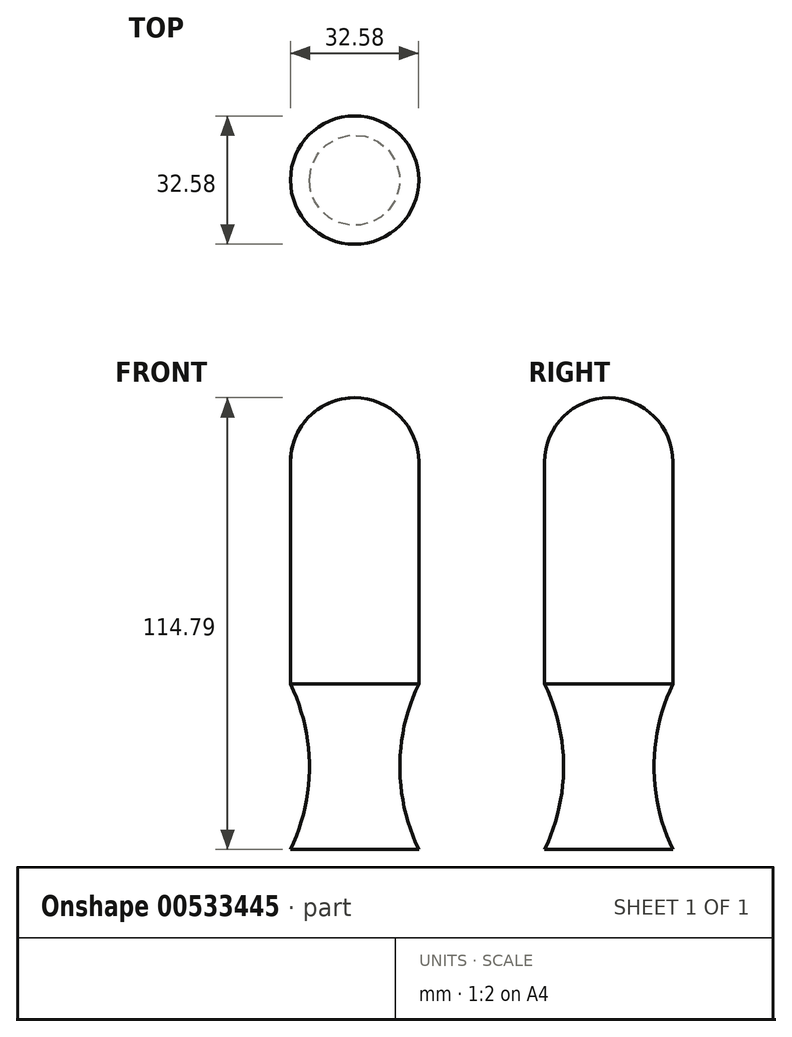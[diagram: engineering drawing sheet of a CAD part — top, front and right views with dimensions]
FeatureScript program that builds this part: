
annotation { "Feature Type Name" : "Feature", "Feature Type Description" : "" }
export const myFeature = defineFeature(function(context is Context, id is Id, definition is map)
    precondition{}
    {
        {
            var Q0;
            Q0=qCreatedBy(makeId("Front.planeOp"),FACE);
            var sketch = newSketch(context, id + "F0", { "sketchPlane" : qUnion([Q0])});
            skLineSegment(sketch, "E0", {"start": v(-16.3, 42.8) * mm, "end": v(-16.3, 0) * mm});
            skLineSegment(sketch, "E1", {"start": v(-16.3, 0) * mm, "end": v(-16.3, -13.62) * mm});
            skArc(sketch, "E2", {"start": v(-16.3, -55.7) * mm, "mid": v(-11.5, -34.65) * mm, "end": v(-16.3, -13.62) * mm});
            skLineSegment(sketch, "E3", {"start": v(-16.3, -55.7) * mm, "end": v(0, -55.7) * mm});
            skLineSegment(sketch, "E4", {"start": v(0, -55.7) * mm, "end": v(0, 62.5) * mm});
            skLineSegment(sketch, "E5.MirrorCS", {"start": v(16.3, 42.8) * mm, "end": v(16.3, 0) * mm});
            skArc(sketch, "E6.MirrorCS", {"start": v(16.3, -55.7) * mm, "mid": v(11.5, -34.65) * mm, "end": v(16.3, -13.62) * mm});
            skLineSegment(sketch, "E7.MirrorCS", {"start": v(16.3, -55.7) * mm, "end": v(0, -55.7) * mm});
            skLineSegment(sketch, "E8.MirrorCS", {"start": v(16.3, 0) * mm, "end": v(16.3, -13.62) * mm});
            skArc(sketch, "E9", {"start": v(16.3, 42.8) * mm, "mid": v(0, 59.1) * mm, "end": v(-16.3, 42.8) * mm});
            skSolve(sketch);
        }
        {
            var Q0;
            {var subQ1=sQuery(id+"F0.wireOp",EDGE,"E0");Q0=makeQuery(id+"F0.imprint","IMPRINT",FACE,{"disambiguationData":[TD([[makeQuery(id+"F0.imprint","IMPRINT",EDGE,{"derivedFrom":subQ1}),1.0]])]});}
            var Q1;
            Q1=sQuery(id+"F0.wireOp",EDGE,"E4");
            revolve(context, id + "F1", {"entities" : qUnion([Q0]), "axis" : qUnion([Q1]), "revolveType" : RevolveType.FULL});
        }
    });
